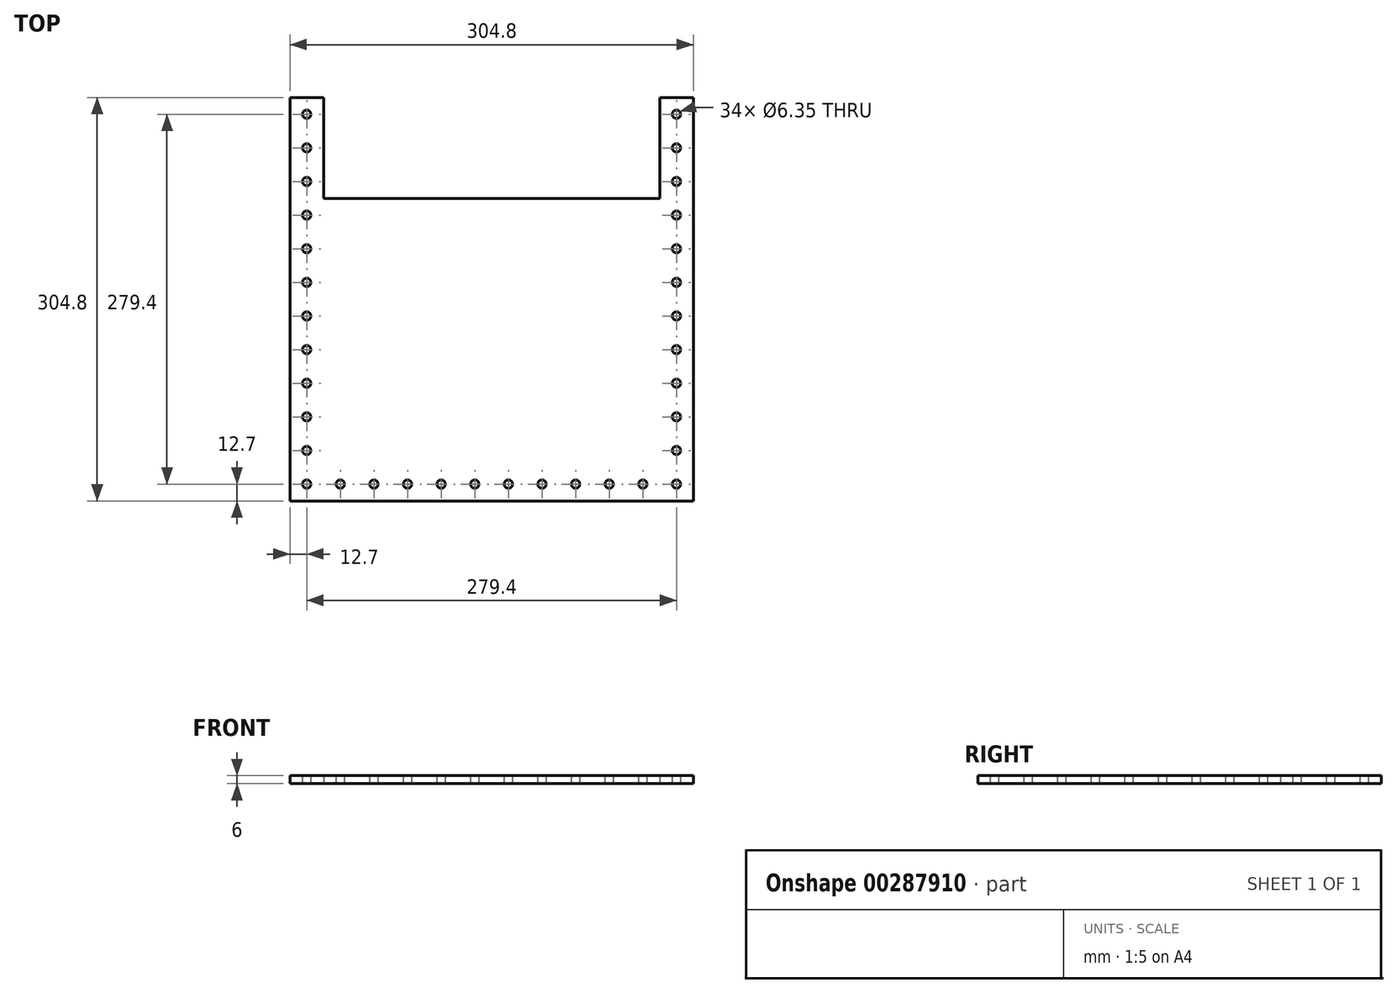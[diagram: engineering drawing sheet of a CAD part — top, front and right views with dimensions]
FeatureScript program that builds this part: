
annotation { "Feature Type Name" : "Feature", "Feature Type Description" : "" }
export const myFeature = defineFeature(function(context is Context, id is Id, definition is map)
    precondition{}
    {
        {
            var Q0;
            Q0=qCreatedBy(makeId("Top.planeOp"),FACE);
            var sketch = newSketch(context, id + "F0", { "sketchPlane" : qUnion([Q0])});
            skLineSegment(sketch, "E0.bottom", {"start": v(152.4, 152.4) * mm, "end": v(-152.4, 152.4) * mm, "construction": true});
            skLineSegment(sketch, "E0.top", {"start": v(152.4, -152.4) * mm, "end": v(-152.4, -152.4) * mm, "construction": true});
            skLineSegment(sketch, "E0.left", {"start": v(152.4, 152.4) * mm, "end": v(152.4, -152.4) * mm, "construction": true});
            skLineSegment(sketch, "E0.right", {"start": v(-152.4, 152.4) * mm, "end": v(-152.4, -152.4) * mm, "construction": true});
            skPoint(sketch, "E0.middle", {"position": v(0, 0) * mm});
            skLineSegment(sketch, "E1", {"start": v(-152.4, 152.4) * mm, "end": v(-127, 152.4) * mm});
            skLineSegment(sketch, "E2", {"start": v(-127, 152.4) * mm, "end": v(-127, 76.2) * mm});
            skLineSegment(sketch, "E3", {"start": v(-127, 76.2) * mm, "end": v(127, 76.2) * mm});
            skLineSegment(sketch, "E4", {"start": v(127, 76.2) * mm, "end": v(127, 152.4) * mm});
            skLineSegment(sketch, "E5", {"start": v(127, 152.4) * mm, "end": v(152.4, 152.4) * mm});
            skLineSegment(sketch, "E6", {"start": v(152.4, -152.4) * mm, "end": v(152.4, 152.4) * mm});
            skLineSegment(sketch, "E7", {"start": v(152.4, -152.4) * mm, "end": v(-152.4, -152.4) * mm});
            skLineSegment(sketch, "E8", {"start": v(-152.4, -152.4) * mm, "end": v(-152.4, 152.4) * mm});
            skSolve(sketch);
        }
        {
            var Q0;
            Q0 = qSketchRegion(id + "F0", true);
            extrude(context, id + "F1", {"entities" : qUnion([Q0]), "depth" : 6 * mm});
        }
        {
            var Q0;
            Q0=makeQuery(id+"F1.opExtrude","CAP_FACE",FACE,{"disambiguationData":[OSD([sQuery(id+"F0.wireOp",EDGE,"E1"),sQuery(id+"F0.wireOp",EDGE,"E2"),sQuery(id+"F0.wireOp",EDGE,"E3"),sQuery(id+"F0.wireOp",EDGE,"E4"),sQuery(id+"F0.wireOp",EDGE,"E5"),sQuery(id+"F0.wireOp",EDGE,"E6"),sQuery(id+"F0.wireOp",EDGE,"E7"),sQuery(id+"F0.wireOp",EDGE,"E8")])],"isStart":false});
            var sketch = newSketch(context, id + "F2", { "sketchPlane" : qUnion([Q0])});
            skCircle(sketch, "E9", {"center": v(-139.7, 139.7) * mm, "radius": 2.55 * mm});
            skCircle(sketch, "E10.0.1.0", {"center": v(-139.7, 114.3) * mm, "radius": 2.55 * mm});
            skCircle(sketch, "E10.0.2.0", {"center": v(-139.7, 88.9) * mm, "radius": 2.55 * mm});
            skCircle(sketch, "E10.0.3.0", {"center": v(-139.7, 63.5) * mm, "radius": 2.55 * mm});
            skCircle(sketch, "E10.0.4.0", {"center": v(-139.7, 38.1) * mm, "radius": 2.55 * mm});
            skCircle(sketch, "E10.0.5.0", {"center": v(-139.7, 12.7) * mm, "radius": 2.55 * mm});
            skCircle(sketch, "E10.0.6.0", {"center": v(-139.7, -12.7) * mm, "radius": 2.55 * mm});
            skCircle(sketch, "E10.0.7.0", {"center": v(-139.7, -38.1) * mm, "radius": 2.55 * mm});
            skCircle(sketch, "E10.0.8.0", {"center": v(-139.7, -63.5) * mm, "radius": 2.55 * mm});
            skCircle(sketch, "E10.0.9.0", {"center": v(-139.7, -88.9) * mm, "radius": 2.55 * mm});
            skCircle(sketch, "E10.0.10.0", {"center": v(-139.7, -114.3) * mm, "radius": 2.55 * mm});
            skCircle(sketch, "E10.0.11.0", {"center": v(-139.7, -139.7) * mm, "radius": 2.55 * mm});
            skCircle(sketch, "E10.1.0.0", {"center": v(139.7, 139.7) * mm, "radius": 2.55 * mm});
            skCircle(sketch, "E10.1.1.0", {"center": v(139.7, 114.3) * mm, "radius": 2.55 * mm});
            skCircle(sketch, "E10.1.2.0", {"center": v(139.7, 88.9) * mm, "radius": 2.55 * mm});
            skCircle(sketch, "E10.1.3.0", {"center": v(139.7, 63.5) * mm, "radius": 2.55 * mm});
            skCircle(sketch, "E10.1.4.0", {"center": v(139.7, 38.1) * mm, "radius": 2.55 * mm});
            skCircle(sketch, "E10.1.5.0", {"center": v(139.7, 12.7) * mm, "radius": 2.55 * mm});
            skCircle(sketch, "E10.1.6.0", {"center": v(139.7, -12.7) * mm, "radius": 2.55 * mm});
            skCircle(sketch, "E10.1.7.0", {"center": v(139.7, -38.1) * mm, "radius": 2.55 * mm});
            skCircle(sketch, "E10.1.8.0", {"center": v(139.7, -63.5) * mm, "radius": 2.55 * mm});
            skCircle(sketch, "E10.1.9.0", {"center": v(139.7, -88.9) * mm, "radius": 2.55 * mm});
            skCircle(sketch, "E10.1.10.0", {"center": v(139.7, -114.3) * mm, "radius": 2.55 * mm});
            skCircle(sketch, "E10.1.11.0", {"center": v(139.7, -139.7) * mm, "radius": 2.55 * mm});
            skLineSegment(sketch, "E10.direction1", {"start": v(-139.7, 139.7) * mm, "end": v(139.7, 139.7) * mm, "construction": true});
            skLineSegment(sketch, "E10.direction2", {"start": v(-139.7, 139.7) * mm, "end": v(-139.7, 114.3) * mm, "construction": true});
            skCircle(sketch, "E11.1.0.0", {"center": v(-114.3, -139.7) * mm, "radius": 2.55 * mm});
            skCircle(sketch, "E11.2.0.0", {"center": v(-88.9, -139.7) * mm, "radius": 2.55 * mm});
            skCircle(sketch, "E11.3.0.0", {"center": v(-63.5, -139.7) * mm, "radius": 2.55 * mm});
            skCircle(sketch, "E11.4.0.0", {"center": v(-38.1, -139.7) * mm, "radius": 2.55 * mm});
            skCircle(sketch, "E11.5.0.0", {"center": v(-12.7, -139.7) * mm, "radius": 2.55 * mm});
            skCircle(sketch, "E11.6.0.0", {"center": v(12.7, -139.7) * mm, "radius": 2.55 * mm});
            skCircle(sketch, "E11.7.0.0", {"center": v(38.1, -139.7) * mm, "radius": 2.55 * mm});
            skCircle(sketch, "E11.8.0.0", {"center": v(63.5, -139.7) * mm, "radius": 2.55 * mm});
            skCircle(sketch, "E11.9.0.0", {"center": v(88.9, -139.7) * mm, "radius": 2.55 * mm});
            skCircle(sketch, "E11.10.0.0", {"center": v(114.3, -139.7) * mm, "radius": 2.55 * mm});
            skLineSegment(sketch, "E11.direction1", {"start": v(-139.7, -139.7) * mm, "end": v(-114.3, -139.7) * mm, "construction": true});
            skSolve(sketch);
        }
        {
            var Q0;
            Q0=sQuery(id+"F2.wireOp",VERTEX,"E10.direction2.end");
            var Q1;
            Q1=sQuery(id+"F2.wireOp",VERTEX,"E11.8.0.0.center");
            var Q2;
            Q2=sQuery(id+"F2.wireOp",VERTEX,"E10.0.5.0.center");
            var Q3;
            Q3=sQuery(id+"F2.wireOp",VERTEX,"E10.1.6.0.center");
            var Q4;
            Q4=sQuery(id+"F2.wireOp",VERTEX,"E10.1.1.0.center");
            var Q5;
            Q5=sQuery(id+"F2.wireOp",VERTEX,"E10.0.8.0.center");
            var Q6;
            Q6=sQuery(id+"F2.wireOp",VERTEX,"E11.7.0.0.center");
            var Q7;
            Q7=sQuery(id+"F2.wireOp",VERTEX,"E10.1.2.0.center");
            var Q8;
            Q8=sQuery(id+"F2.wireOp",VERTEX,"E11.4.0.0.center");
            var Q9;
            Q9=sQuery(id+"F2.wireOp",VERTEX,"E10.0.7.0.center");
            var Q10;
            Q10=sQuery(id+"F2.wireOp",VERTEX,"E11.2.0.0.center");
            var Q11;
            Q11=sQuery(id+"F2.wireOp",VERTEX,"E11.direction1.end");
            var Q12;
            Q12=sQuery(id+"F2.wireOp",VERTEX,"E11.6.0.0.center");
            var Q13;
            Q13=sQuery(id+"F2.wireOp",VERTEX,"E9.center");
            var Q14;
            Q14=sQuery(id+"F2.wireOp",VERTEX,"E10.0.10.0.center");
            var Q15;
            Q15=sQuery(id+"F2.wireOp",VERTEX,"E10.1.5.0.center");
            var Q16;
            Q16=sQuery(id+"F2.wireOp",VERTEX,"E10.1.4.0.center");
            var Q17;
            Q17=sQuery(id+"F2.wireOp",VERTEX,"E10.1.7.0.center");
            var Q18;
            Q18=sQuery(id+"F2.wireOp",VERTEX,"E10.1.0.0.center");
            var Q19;
            Q19=sQuery(id+"F2.wireOp",VERTEX,"E11.9.0.0.center");
            var Q20;
            Q20=sQuery(id+"F2.wireOp",VERTEX,"E10.0.11.0.center");
            var Q21;
            Q21=sQuery(id+"F2.wireOp",VERTEX,"E11.3.0.0.center");
            var Q22;
            Q22=sQuery(id+"F2.wireOp",VERTEX,"E11.5.0.0.center");
            var Q23;
            Q23=sQuery(id+"F2.wireOp",VERTEX,"E10.1.11.0.center");
            var Q24;
            Q24=sQuery(id+"F2.wireOp",VERTEX,"E10.1.10.0.center");
            var Q25;
            Q25=sQuery(id+"F2.wireOp",VERTEX,"E10.0.4.0.center");
            var Q26;
            Q26=sQuery(id+"F2.wireOp",VERTEX,"E10.1.9.0.center");
            var Q27;
            Q27=sQuery(id+"F2.wireOp",VERTEX,"E10.1.8.0.center");
            var Q28;
            Q28=sQuery(id+"F2.wireOp",VERTEX,"E10.0.6.0.center");
            var Q29;
            Q29=sQuery(id+"F2.wireOp",VERTEX,"E10.0.3.0.center");
            var Q30;
            Q30=sQuery(id+"F2.wireOp",VERTEX,"E10.1.3.0.center");
            var Q31;
            Q31=sQuery(id+"F2.wireOp",VERTEX,"E10.0.9.0.center");
            var Q32;
            Q32=sQuery(id+"F2.wireOp",VERTEX,"E10.0.2.0.center");
            var Q33;
            Q33=sQuery(id+"F2.wireOp",VERTEX,"E11.10.0.0.center");
            var Q34;
            Q34=makeQuery(id+"F1.opExtrude","SWEPT_BODY",BODY,{"disambiguationData":[OSD([sQuery(id+"F0.wireOp",EDGE,"E1"),sQuery(id+"F0.wireOp",EDGE,"E2"),sQuery(id+"F0.wireOp",EDGE,"E3"),sQuery(id+"F0.wireOp",EDGE,"E4"),sQuery(id+"F0.wireOp",EDGE,"E5"),sQuery(id+"F0.wireOp",EDGE,"E6"),sQuery(id+"F0.wireOp",EDGE,"E7"),sQuery(id+"F0.wireOp",EDGE,"E8")])]});
            hole(context, id + "F3", {"style" : HoleStyle.SIMPLE, "endStyle" : HoleEndStyle.THROUGH, "holeDiameter" : 6.35 * mm, "tappedDepth" : 12.7 * mm, "tapClearance" : 3, "locations" : qUnion([Q0, Q1, Q2, Q3, Q4, Q5, Q6, Q7, Q8, Q9, Q10, Q11, Q12, Q13, Q14, Q15, Q16, Q17, Q18, Q19, Q20, Q21, Q22, Q23, Q24, Q25, Q26, Q27, Q28, Q29, Q30, Q31, Q32, Q33]), "scope" : qUnion([Q34])});
        }
    });
